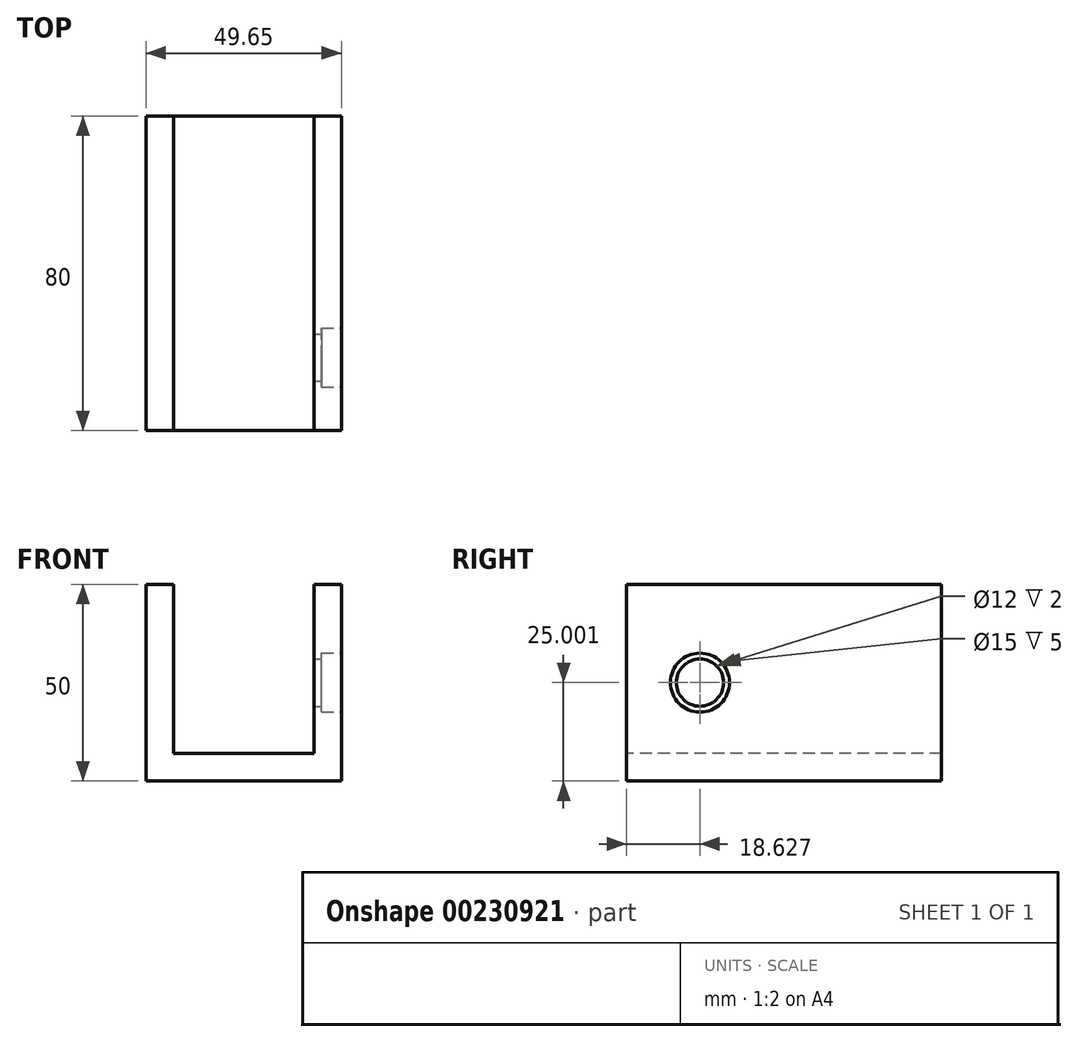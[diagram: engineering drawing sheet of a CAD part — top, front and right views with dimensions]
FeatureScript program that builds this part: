
annotation { "Feature Type Name" : "Feature", "Feature Type Description" : "" }
export const myFeature = defineFeature(function(context is Context, id is Id, definition is map)
    precondition{}
    {
        {
            var Q0;
            Q0=qCreatedBy(makeId("Front.planeOp"),FACE);
            var sketch = newSketch(context, id + "F0", { "sketchPlane" : qUnion([Q0])});
            skLineSegment(sketch, "E0", {"start": v(-24.28, 35.12) * mm, "end": v(-24.28, -14.88) * mm});
            skLineSegment(sketch, "E1", {"start": v(-24.28, -14.88) * mm, "end": v(25.37, -14.88) * mm});
            skLineSegment(sketch, "E2", {"start": v(25.37, -14.88) * mm, "end": v(25.37, 35.12) * mm});
            skLineSegment(sketch, "E3", {"start": v(25.37, 35.12) * mm, "end": v(18.37, 35.12) * mm});
            skLineSegment(sketch, "E4", {"start": v(18.37, 35.12) * mm, "end": v(18.37, -7.88) * mm});
            skLineSegment(sketch, "E5", {"start": v(18.37, -7.88) * mm, "end": v(-17.28, -7.88) * mm});
            skLineSegment(sketch, "E6", {"start": v(-17.28, -7.88) * mm, "end": v(-17.28, 35.12) * mm});
            skLineSegment(sketch, "E7", {"start": v(-17.28, 35.12) * mm, "end": v(-24.28, 35.12) * mm});
            skSolve(sketch);
        }
        {
            var Q0;
            Q0=makeQuery(id+"F0.imprint","IMPRINT",FACE,{"disambiguationData":[TD([[makeQuery(id+"F0.imprint","IMPRINT",EDGE,{"derivedFrom":sQuery(id+"F0.wireOp",EDGE,"E0")}),1.0]])]});
            extrude(context, id + "F1", {"entities" : qUnion([Q0]), "oppositeDirection" : true, "depth" : 80 * mm});
        }
        {
            var Q0;
            Q0=makeQuery(id+"F1.opExtrude","SWEPT_FACE",FACE,{"disambiguationData":[OSD([sQuery(id+"F0.wireOp",EDGE,"E2")])]});
            var sketch = newSketch(context, id + "F2", { "sketchPlane" : qUnion([Q0])});
            skCircle(sketch, "E8", {"center": v(57.16, 10.12) * mm, "radius": 5 * mm});
            skPoint(sketch, "E8.centerSnap0", {"position": v(80, 10.12) * mm});
            skCircle(sketch, "E9", {"center": v(57.16, 20.12) * mm, "radius": 2.5 * mm});
            skCircle(sketch, "E10", {"center": v(57.16, 0.12) * mm, "radius": 2.5 * mm});
            skCircle(sketch, "E11", {"center": v(18.63, 10.12) * mm, "radius": 6 * mm});
            skCircle(sketch, "E12", {"center": v(57.16, 10.12) * mm, "radius": 7.5 * mm});
            skCircle(sketch, "E13", {"center": v(18.63, 10.12) * mm, "radius": 7.5 * mm});
            skSolve(sketch);
        }
        {
            var Q0;
            Q0=makeQuery(id+"F2.imprint","IMPRINT",FACE,{"disambiguationData":[TD([[makeQuery(id+"F2.imprint","IMPRINT",EDGE,{"derivedFrom":sQuery(id+"F2.wireOp",EDGE,"E11")}),1.0]])]});
            var Q1;
            Q1=sQuery(id+"F2.wireOp",EDGE,"E11");
            extrude(context, id + "F3", {"entities" : qUnion([Q0]), "operationType" : NewBodyOperationType.REMOVE, "surfaceEntities" : qUnion([Q1]), "oppositeDirection" : true, "depth" : 25 * mm});
        }
        {
            var Q0;
            Q0=makeQuery(id+"F2.imprint","IMPRINT",FACE,{"disambiguationData":[TD([[makeQuery(id+"F2.imprint","IMPRINT",EDGE,{"derivedFrom":sQuery(id+"F2.wireOp",EDGE,"E11")}),-1.0]])]});
            var Q1;
            Q1=sQuery(id+"F2.wireOp",EDGE,"E13");
            extrude(context, id + "F4", {"entities" : qUnion([Q0]), "operationType" : NewBodyOperationType.REMOVE, "surfaceEntities" : qUnion([Q1]), "oppositeDirection" : true, "depth" : 5 * mm});
        }
    });
